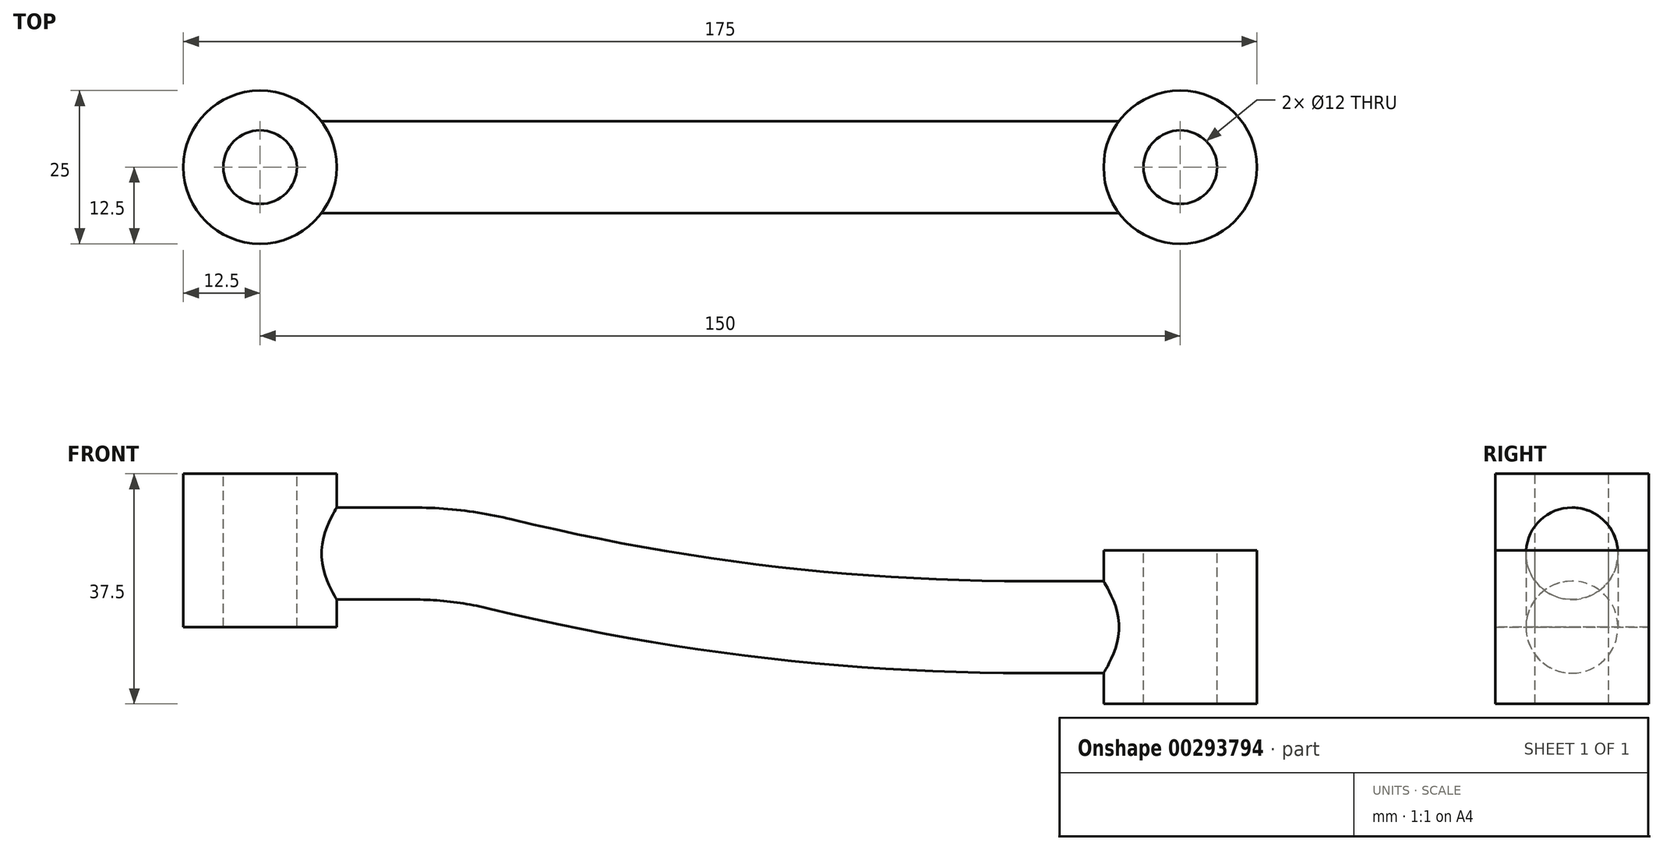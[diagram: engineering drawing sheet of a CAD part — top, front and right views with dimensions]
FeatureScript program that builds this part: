
annotation { "Feature Type Name" : "Feature", "Feature Type Description" : "" }
export const myFeature = defineFeature(function(context is Context, id is Id, definition is map)
    precondition{}
    {
        {
            var Q0;
            Q0=qCreatedBy(makeId("Top.planeOp"),FACE);
            var sketch = newSketch(context, id + "F0", { "sketchPlane" : qUnion([Q0])});
            skCircle(sketch, "E0", {"center": v(0, 0) * mm, "radius": 12.5 * mm});
            skCircle(sketch, "E1", {"center": v(150, 0) * mm, "radius": 12.5 * mm});
            skSolve(sketch);
        }
        {
            var Q0;
            Q0=makeQuery(id+"F0.imprint","IMPRINT",FACE,{"disambiguationData":[TD([[makeQuery(id+"F0.imprint","IMPRINT",EDGE,{"derivedFrom":sQuery(id+"F0.wireOp",EDGE,"E0")}),1.0]])]});
            extrude(context, id + "F1", {"entities" : qUnion([Q0]), "depth" : 25 * mm});
        }
        {
            var Q0;
            Q0=makeQuery(id+"F0.imprint","IMPRINT",FACE,{"disambiguationData":[TD([[makeQuery(id+"F0.imprint","IMPRINT",EDGE,{"derivedFrom":sQuery(id+"F0.wireOp",EDGE,"E1")}),1.0]])]});
            extrude(context, id + "F2", {"entities" : qUnion([Q0]), "endBound" : BoundingType.SYMMETRIC, "depth" : 25 * mm});
        }
        {
            var Q0;
            Q0=qCreatedBy(makeId("Front.planeOp"),FACE);
            var sketch = newSketch(context, id + "F3", { "sketchPlane" : qUnion([Q0])});
            skLineSegment(sketch, "E2", {"start": v(0, 12) * mm, "end": v(25, 12) * mm});
            skArc(sketch, "E3", {"start": v(25, 12) * mm, "mid": v(32.15, 11.57) * mm, "end": v(39.2, 10.3) * mm});
            skArc(sketch, "E4", {"start": v(39.2, 10.3) * mm, "mid": v(81.79, 2.58) * mm, "end": v(125, 0) * mm});
            skLineSegment(sketch, "E5", {"start": v(125, 0) * mm, "end": v(150, 0) * mm});
            skSolve(sketch);
        }
        {
            var Q0;
            Q0=qCreatedBy(makeId("Right.planeOp"),FACE);
            var sketch = newSketch(context, id + "F4", { "sketchPlane" : qUnion([Q0])});
            skCircle(sketch, "E6", {"center": v(0, 12) * mm, "radius": 7.5 * mm});
            skSolve(sketch);
        }
        {
            var Q0;
            Q0 = qSketchRegion(id + "F4", true);
            var Q1;
            Q1=sQuery(id+"F3.wireOp",EDGE,"E2");
            var Q2;
            Q2=sQuery(id+"F3.wireOp",EDGE,"E3");
            var Q3;
            Q3=sQuery(id+"F3.wireOp",EDGE,"E4");
            var Q4;
            Q4=sQuery(id+"F3.wireOp",EDGE,"E5");
            sweep(context, id + "F5", {"operationType" : NewBodyOperationType.ADD, "profiles" : qUnion([Q0]), "path" : qUnion([Q1, Q2, Q3, Q4])});
        }
        {
            var Q0;
            Q0=makeQuery(id+"F1.opExtrude","CAP_FACE",FACE,{"disambiguationData":[OSD([sQuery(id+"F0.wireOp",EDGE,"E0")])],"isStart":false});
            var sketch = newSketch(context, id + "F6", { "sketchPlane" : qUnion([Q0])});
            skCircle(sketch, "E7", {"center": v(0, 0) * mm, "radius": 6 * mm});
            skCircle(sketch, "E8", {"center": v(150, 0) * mm, "radius": 6 * mm});
            skSolve(sketch);
        }
        {
            var Q0;
            Q0 = qSketchRegion(id + "F6", true);
            extrude(context, id + "F7", {"entities" : qUnion([Q0]), "operationType" : NewBodyOperationType.REMOVE, "endBound" : BoundingType.THROUGH_ALL, "oppositeDirection" : true, "depth" : 25 * mm});
        }
    });
